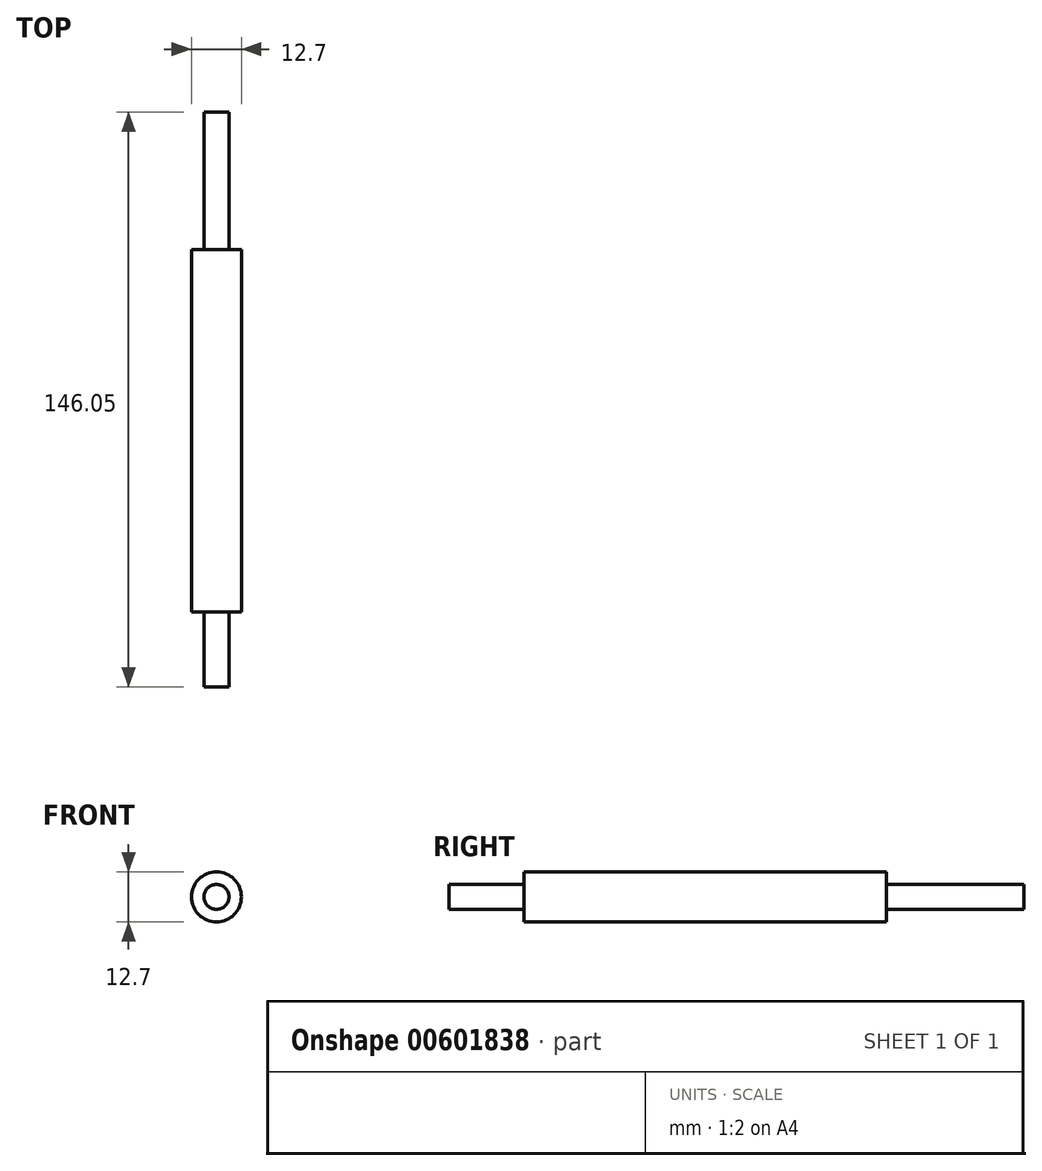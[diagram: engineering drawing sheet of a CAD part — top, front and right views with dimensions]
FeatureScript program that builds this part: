
annotation { "Feature Type Name" : "Feature", "Feature Type Description" : "" }
export const myFeature = defineFeature(function(context is Context, id is Id, definition is map)
    precondition{}
    {
        {
            var Q0;
            Q0=qCreatedBy(makeId("Right.planeOp"),FACE);
            var sketch = newSketch(context, id + "F0", { "sketchPlane" : qUnion([Q0])});
            skLineSegment(sketch, "E0", {"start": v(-72, 0) * mm, "end": v(-72, 3.17) * mm});
            skLineSegment(sketch, "E1", {"start": v(-72, 3.17) * mm, "end": v(-52.96, 3.17) * mm});
            skLineSegment(sketch, "E2", {"start": v(-52.96, 3.17) * mm, "end": v(-52.96, 6.35) * mm});
            skLineSegment(sketch, "E3", {"start": v(-52.96, 6.35) * mm, "end": v(39.12, 6.35) * mm});
            skLineSegment(sketch, "E4", {"start": v(39.12, 6.35) * mm, "end": v(39.12, 3.17) * mm});
            skLineSegment(sketch, "E5", {"start": v(39.12, 3.17) * mm, "end": v(74.04, 3.18) * mm});
            skLineSegment(sketch, "E6", {"start": v(74.04, 3.18) * mm, "end": v(74.04, 0) * mm});
            skLineSegment(sketch, "E7", {"start": v(74.04, 0) * mm, "end": v(-72, 0) * mm});
            skSolve(sketch);
        }
        {
            var Q0;
            Q0=makeQuery(id+"F0.imprint","IMPRINT",FACE,{"disambiguationData":[TD([[makeQuery(id+"F0.imprint","IMPRINT",EDGE,{"derivedFrom":sQuery(id+"F0.wireOp",EDGE,"E0")}),-1.0]])]});
            var Q1;
            Q1=sQuery(id+"F0.wireOp",EDGE,"E7");
            revolve(context, id + "F1", {"entities" : qUnion([Q0]), "axis" : qUnion([Q1]), "revolveType" : RevolveType.FULL});
        }
    });
